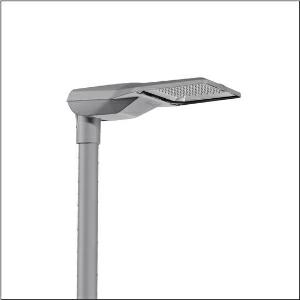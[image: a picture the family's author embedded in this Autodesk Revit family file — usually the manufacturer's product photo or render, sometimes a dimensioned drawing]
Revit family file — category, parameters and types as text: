
# Revit family: streetlight_sl_21_iq_midi___stw1_0a_5xe3e31d08nb_8d25
name_source: partatom
category: Lighting Fixtures
units: mm (PartAtom-declared; Revit-internal decimal feet)

## family parameters
Cut with Voids When Loaded = No
Host = Face
Light Source = No
Part Type = Normal
Room Calculation Point = No
Round Connector Dimension = Use Diameter
Shared = No

## types (1)
- --- (1 x LED, 23230 lm, 155.5 W, 3000K)
    Apparent Load = 155 VA
    CIE Flux Codes = 39 75 98 100 100
    Color Rendering = 70
    Color Temperature = 3000K
    Default Elevation = 1800 mm
    Description = Streetlight SL 21 iQ midi, mast luminaire, primary light control with lens, of PMMA, primary optical cover: cover, of toughened safety glass, transparent, light distribution: STW1.0a, light emission: direct distribution, primary light characteristic: asymmetric, installation type: post-top, side-entry, LED, High Power LED, rated luminous flux: 23.230lm, luminous efficacy: 149lm/W, light colour: 730, colour temperature: 3000K, control: Auto-Match, Temp-Guard, Lumen-Switch, Night-Set, Smart-Wire, Light-Fading, Desk-Remote (wireless, voltage-free reading and setting of iQ features in the workshop via application-optimized NFC function/RFID function), optimised constant luminous flux control (CLO 2.0), presetting dimming linear, mains connection: 230..240V, AC, 50/60Hz, start of lifetime: 156W, end of service life: 162W, reduction: 69W, luminaire housing, of diecast aluminium, powder-coated, Siteco® metallic grey (DB 702S), corrosivity category C5 mid according to DIN EN ISO 12944, please order mast flange separately, inclination adjustable: 0°, 5°, 10°, 15°, sealing non-destructively replaceable, multi-level sealing system, length: 644mm, width: 335mm, height: 110mm, mast flange for spigot size: 42mm (side-entry): 5XC10008XM4, 60/48mm (side-entry/post-top): 5XC10108XM2, 76/60mm (side-entry/post-top): 5XC10108XM1, protection rating (complete): IP66, insulation class (complete): insulation class II (safety insulation), certification: CE, ENEC, ENEC+, VDE, impact resistance: IK09, permissible operating ambient temperature for outdoor applications: -40..+50°C, standard-compliant lighting for roads and squares, packaging unit: 1 piece

Light Distribution: STW1.0a
    Height = 111 mm
    Lamp = 1 x LED
    Lamp Light Flux = 23230 lm
    Lamp Power = 155.5 W
    Lamp count = 1
    Length = 644 mm
    Luminous efficacy = 149 lm/W
    Manufacturer = Siteco
    ModVariant = No
    Model = 5XE3E31D08NB
    Number of Poles = 1
    OnlyDefault = Yes
    Power Factor = 1
    Product Name = Streetlight SL 21 iQ midi | STW1.0a
    Product group = mast luminaire | pylon top
    ProductGroupID = 6100
    Protection Class = Protection class II
    Protection Degree = IP 66
    RLX_Detail_Level = 1
    RLX_Emergency_Light_Flux = 0 lm
    RLX_Emergency_Type = 0
    RLX_Emergency_Type_DB = No
    RlxData = <blob elided: 91245 chars, md5=2aac71dc>
    Socket = socket
    Standby Power = 0 W
    System Light Flux = 23230 lm
    System Power = 155 W
    Type Comments = factory setting: luminous flux: 100 % | dim-lin: 254 | 823 mA
    Type Image = l_1004298.jpg
    URL = http://relux.com
    VarID = @adj_102505
    Voltage = 0 V
    Weight = 0.00 kg
    Width = 336 mm

## geometry (parser evidence)
native form markers: Blend x4, Sweep x10
no freeform markers — native parametric forms only
